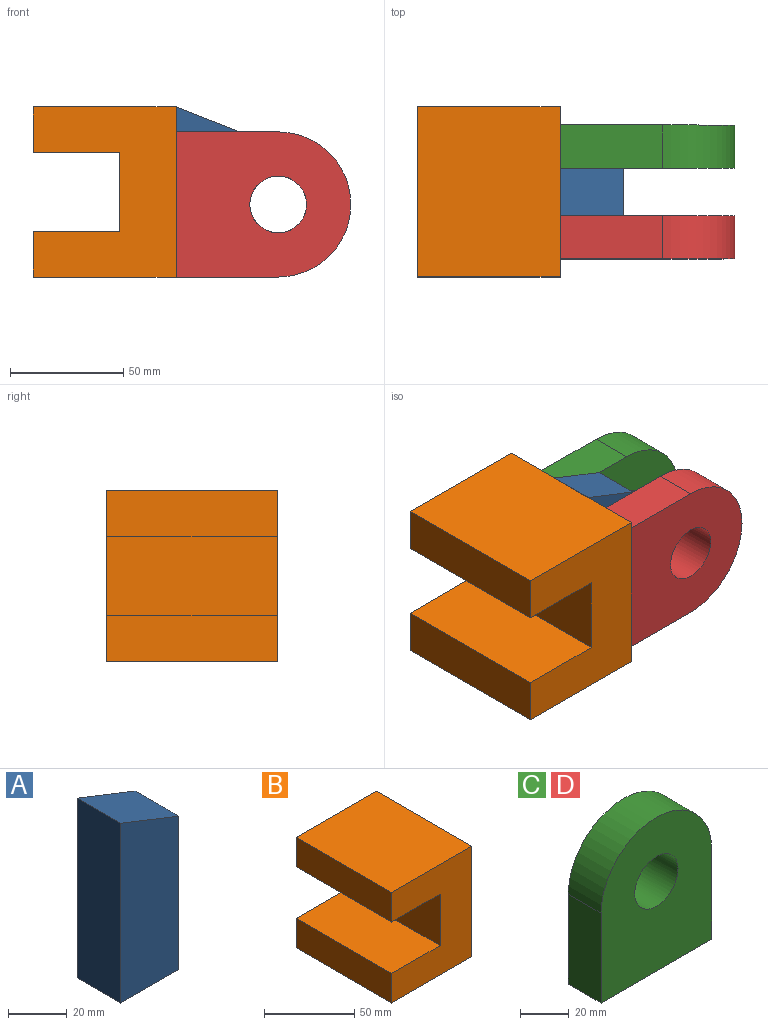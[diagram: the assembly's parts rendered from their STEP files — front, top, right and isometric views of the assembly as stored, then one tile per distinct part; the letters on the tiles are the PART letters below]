
ASSEMBLY  parts=4 mates=3
PART A: 6 faces, bbox 28x21x75 mm
  f0: plane 75x21mm, normal (-1,0,0), area 1575mm2, adj f1,f3,f4,f5
  f1: plane 28x21mm, normal (0,0,-1), area 588mm2, adj f0,f2,f4,f5
  f2: plane 64x21mm, normal (1,0,0), area 1344mm2, adj f1,f3,f4,f5
  f3: plane 28x21mm, normal (0.37,0,0.93), area 631.7mm2, adj f0,f2,f4,f5
  f4: plane 75x28mm, normal (0,1,0), area 1946mm2, adj f0,f1,f2,f3
  f5: plane 75x28mm, normal (0,-1,0), area 1946mm2, adj f0,f1,f2,f3
PART B: 10 faces, bbox 63x75x75 mm
  f0: plane 75x20mm, normal (-1,0,0), area 1500mm2, adj f1,f4,f5,f9
  f1: plane 75x63mm, normal (0,-1,0), area 3395mm2, adj f0,f2,f3,f5,f6,f7,f8,f9
  f2: plane 75x20mm, normal (-1,0,0), area 1500mm2, adj f1,f4,f6,f7
  f3: plane 75x75mm, normal (1,0,0), area 5625mm2, adj f1,f4,f5,f6
  f4: plane 75x63mm, normal (0,1,0), area 3395mm2, adj f0,f2,f3,f5,f6,f7,f8,f9
  f5: plane 75x63mm, normal (0,0,1), area 4725mm2, adj f0,f1,f3,f4
  f6: plane 75x63mm, normal (0,0,-1), area 4725mm2, adj f1,f2,f3,f4
  f7: plane 75x38mm, normal (0,0,1), area 2850mm2, adj f1,f2,f4,f8
  f8: plane 75x35mm, normal (-1,0,0), area 2625mm2, adj f1,f4,f7,f9
  f9: plane 75x38mm, normal (0,0,-1), area 2850mm2, adj f0,f1,f4,f8
PART C: 7 faces, bbox 64x19x77 mm
  f0: cylinder r=32mm len=64mm, axis (0,1,0), area 1910.1mm2, adj f1,f2,f3,f4
  f1: plane 77x64mm, normal (0,-1,0), area 3997.6mm2, adj f0,f3,f4,f5,f6
  f2: plane 77x64mm, normal (0,1,0), area 3997.6mm2, adj f0,f3,f4,f5,f6
  f3: plane 45x19mm, normal (1,0,0), area 855mm2, adj f0,f1,f2,f5
  f4: plane 45x19mm, normal (-1,0,0), area 855mm2, adj f0,f1,f2,f5
  f5: plane 64x19mm, normal (0,0,-1), area 1216mm2, adj f1,f2,f3,f4
  f6: cylinder r=12.5mm len=25mm, axis (0,1,0), area 1492.3mm2, adj f1,f2
PART D: same geometry as C
PLACE A t=(98.92,106.94,-9.25)mm
PLACE B t=(35.92,79.94,-9.25)mm
PLACE C rot(axis=(0,1,0),90deg) t=(143.92,146.94,22.75)mm
PLACE D rot(axis=(0,1,0),90deg) t=(143.92,106.94,22.75)mm
MATE planar D.f2 <-> A.f5  axis (0,1,0) through (98.92,106.94,-9.25)mm
MATE planar B.f3 <-> A.f0  axis (1,0,0) through (98.92,117.44,28.25)mm
MATE planar C.f1 <-> A.f4  axis (0,-1,0) through (98.92,127.94,-9.25)mm
